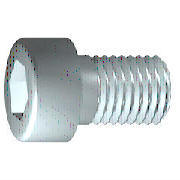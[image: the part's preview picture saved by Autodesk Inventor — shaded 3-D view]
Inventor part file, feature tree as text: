
AUTODESK INVENTOR PART (.ipt)
format: ipt  version: 2020 (Build 240168000, 168)  size: 194,048 bytes
history: native  units: mm (DEFAULTED — no unit token found)
features: sketch x2, extrude x1, plane x1, fillet x1
ambient origin geometry x7: Origin, YZ Plane, XY Plane, X Axis, Y Axis, Z Axis, Center Point
bodies: Solid1 (feature_tree), Body (feature_tree)
feature tree (5):
  extrude  "Slot"  Depth=3.5mm
  plane  "Work Plane1"
  fillet  "Fillet2"  Radius=3.5mm
  sketch  "Sketch1"  dims[d1=22.6mm d2=0.49086mm d3=3.5mm]
  sketch  "Sketch2"  dims[d4=2.7mm d5=60.0deg d6=5.0mm d7=5.0mm d8=3.464102mm d9=8.5mm d10=90.0deg d11=10.0mm d12=0.0mm d13=22.6mm d14=0.0mm d15=0.49076mm d16=0.49076mm d17=0.5mm d19=0.0mm d26=25.0mm d27=45.0deg d28=0.0mm d29=0.0mm d30=0.1mm]
